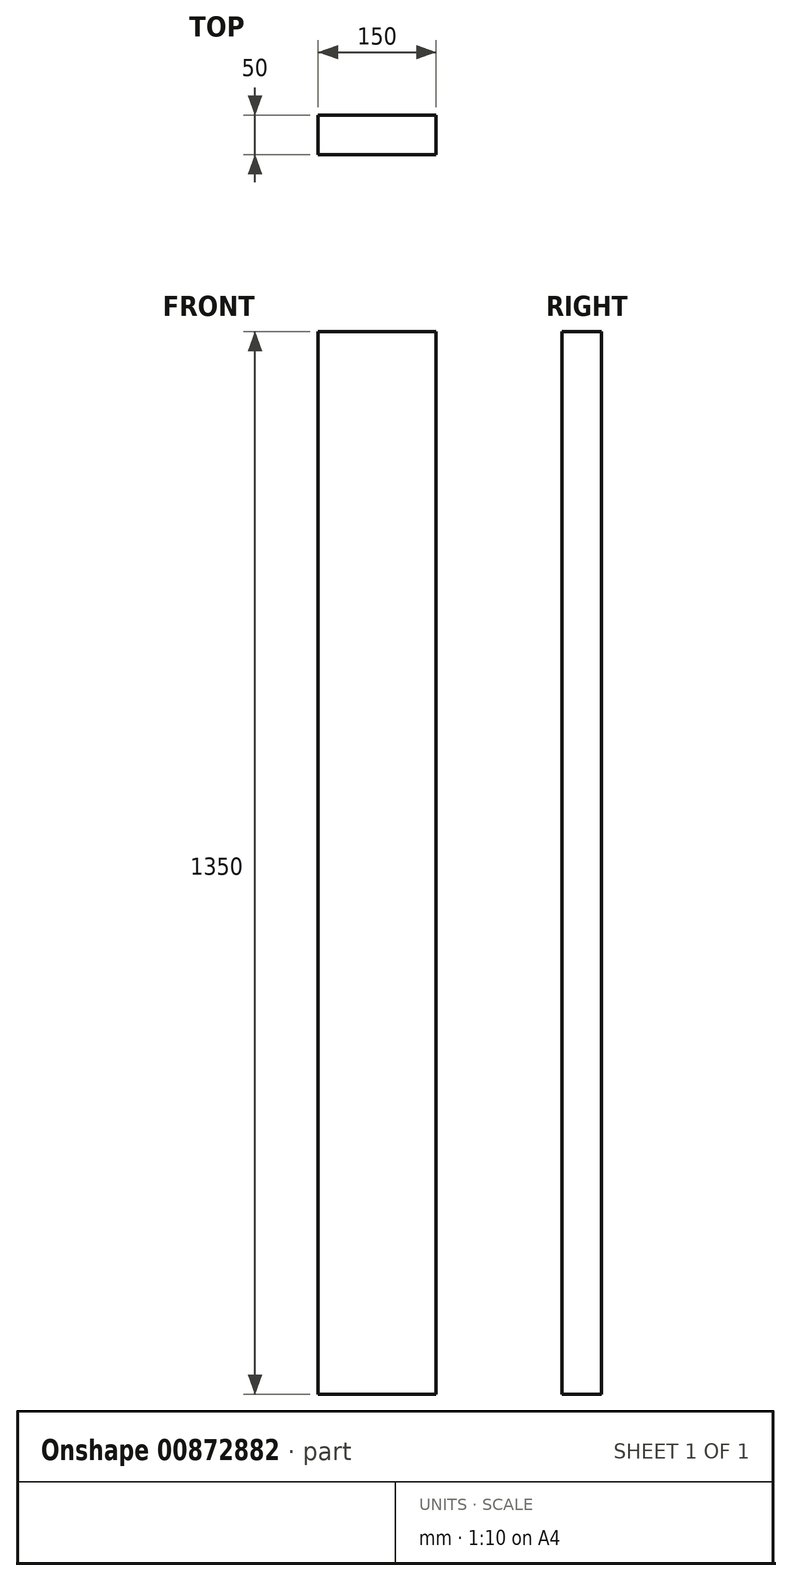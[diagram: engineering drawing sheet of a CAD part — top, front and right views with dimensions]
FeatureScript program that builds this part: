
annotation { "Feature Type Name" : "Feature", "Feature Type Description" : "" }
export const myFeature = defineFeature(function(context is Context, id is Id, definition is map)
    precondition{}
    {
        {
            var Q0;
            Q0=qCreatedBy(makeId("Top.planeOp"),FACE);
            var sketch = newSketch(context, id + "F0", { "sketchPlane" : qUnion([Q0])});
            skLineSegment(sketch, "E0.bottom", {"start": v(0, 3.2) * mm, "end": v(150, 3.2) * mm});
            skLineSegment(sketch, "E0.top", {"start": v(0, -46.8) * mm, "end": v(150, -46.8) * mm});
            skLineSegment(sketch, "E0.left", {"start": v(0, 3.2) * mm, "end": v(0, -46.8) * mm});
            skLineSegment(sketch, "E0.right", {"start": v(150, 3.2) * mm, "end": v(150, -46.8) * mm});
            skSolve(sketch);
        }
        {
            var Q0;
            Q0=makeQuery(id+"F0.imprint","IMPRINT",FACE,{"disambiguationData":[TD([[makeQuery(id+"F0.imprint","IMPRINT",EDGE,{"derivedFrom":sQuery(id+"F0.wireOp",EDGE,"E0.bottom")}),-1.0]])]});
            extrude(context, id + "F1", {"entities" : qUnion([Q0]), "depth" : (1600 - 250) * mm, "offsetDistance" : 25 * mm});
        }
    });
